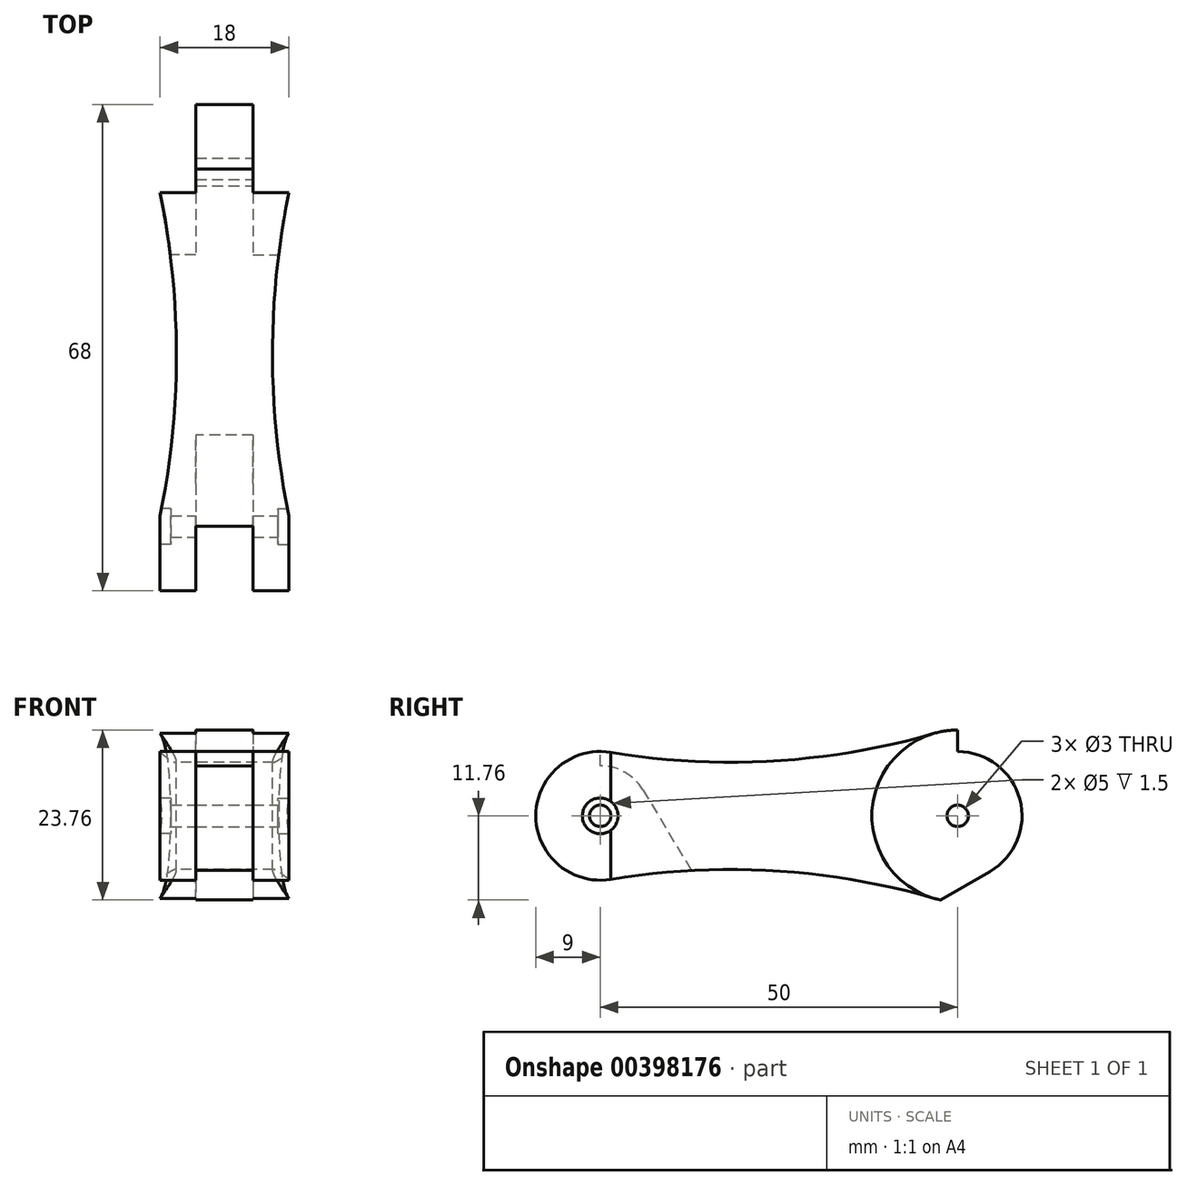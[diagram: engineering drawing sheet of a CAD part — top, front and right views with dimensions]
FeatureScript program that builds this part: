
annotation { "Feature Type Name" : "Feature", "Feature Type Description" : "" }
export const myFeature = defineFeature(function(context is Context, id is Id, definition is map)
    precondition{}
    {
        {
            var Q0;
            Q0=qCreatedBy(makeId("Right.planeOp"),FACE);
            var sketch = newSketch(context, id + "F0", { "sketchPlane" : qUnion([Q0])});
            skArc(sketch, "E0", {"start": v(1.47, 8.88) * mm, "mid": v(-9, 0) * mm, "end": v(1.47, -8.88) * mm});
            skLineSegment(sketch, "E1", {"start": v(-29.92, 0) * mm, "end": v(87.26, 0) * mm, "construction": true});
            skArc(sketch, "E2", {"start": v(46.67, -11.53) * mm, "mid": v(62, 0) * mm, "end": v(46.67, 11.53) * mm});
            skArc(sketch, "E3", {"start": v(1.47, 8.88) * mm, "mid": v(24.22, 7.68) * mm, "end": v(46.67, 11.53) * mm});
            skArc(sketch, "E4", {"start": v(46.67, -11.53) * mm, "mid": v(24.22, -7.68) * mm, "end": v(1.47, -8.88) * mm});
            skSolve(sketch);
        }
        {
            var Q0;
            Q0=qSketchRegion(id+"F0",true);
            extrude(context, id + "F1", {"entities" : qUnion([Q0]), "depth" : 5 * mm});
        }
        {
            var Q0;
            Q0=makeQuery(id+"F1.opExtrude","CAP_FACE",FACE,{"disambiguationData":[OSD([sQuery(id+"F0.wireOp",EDGE,"E0"),sQuery(id+"F0.wireOp",EDGE,"E2"),sQuery(id+"F0.wireOp",EDGE,"E3"),sQuery(id+"F0.wireOp",EDGE,"E4")])],"isStart":false});
            var sketch = newSketch(context, id + "F2", { "sketchPlane" : qUnion([Q0])});
            skArc(sketch, "E5.0", {"start": v(1.47, 8.88) * mm, "mid": v(24.22, 7.68) * mm, "end": v(46.67, 11.53) * mm});
            skArc(sketch, "E6.0", {"start": v(1.47, 8.88) * mm, "mid": v(0.74, 8.97) * mm, "end": v(0, 9) * mm});
            skArc(sketch, "E7.0", {"start": v(46.67, -11.53) * mm, "mid": v(29.88, -8.17) * mm, "end": v(12.76, -7.65) * mm});
            skArc(sketch, "E8.0", {"start": v(46.67, -11.53) * mm, "mid": v(62, 0) * mm, "end": v(46.67, 11.53) * mm});
            skArc(sketch, "E9", {"start": v(7, 0) * mm, "mid": v(4.95, 4.95) * mm, "end": v(0, 7) * mm});
            skLineSegment(sketch, "E10", {"start": v(0, 7) * mm, "end": v(0, 9) * mm});
            skLineSegment(sketch, "E11", {"start": v(0, 0) * mm, "end": v(34.92, 0) * mm, "construction": true});
            skLineSegment(sketch, "E12", {"start": v(6, 3.6) * mm, "end": v(12.76, -7.65) * mm});
            skPoint(sketch, "E13.orphan", {"position": v(7, 0) * mm});
            skSolve(sketch);
        }
        {
            var Q0;
            Q0=qSketchRegion(id+"F2",true);
            extrude(context, id + "F3", {"entities" : qUnion([Q0]), "operationType" : NewBodyOperationType.ADD, "depth" : 8 * mm});
        }
        {
            var Q0;
            Q0=makeQuery(id+"F3.opExtrude","CAP_FACE",FACE,{"disambiguationData":[OSD([sQuery(id+"F2.wireOp",EDGE,"E5.0"),sQuery(id+"F2.wireOp",EDGE,"E6.0"),sQuery(id+"F2.wireOp",EDGE,"E7.0"),sQuery(id+"F2.wireOp",EDGE,"E8.0"),sQuery(id+"F2.wireOp",EDGE,"E9"),sQuery(id+"F2.wireOp",EDGE,"E10"),sQuery(id+"F2.wireOp",EDGE,"JRJ70NO1-7vJe-Li3z-EIXT-plhISmGAnEbH")])],"isStart":false});
            var sketch = newSketch(context, id + "F4", { "sketchPlane" : qUnion([Q0])});
            skArc(sketch, "E14.0", {"start": v(0, 9) * mm, "mid": v(-8.97, -0.74) * mm, "end": v(1.47, -8.88) * mm});
            skArc(sketch, "E15.0", {"start": v(1.47, 8.88) * mm, "mid": v(24.22, 7.68) * mm, "end": v(46.67, 11.53) * mm});
            skArc(sketch, "E16.0", {"start": v(12.76, -7.65) * mm, "mid": v(7.1, -8.1) * mm, "end": v(1.47, -8.88) * mm});
            skArc(sketch, "E17.0", {"start": v(46.67, -11.53) * mm, "mid": v(29.88, -8.17) * mm, "end": v(12.76, -7.65) * mm});
            skArc(sketch, "E18.0", {"start": v(46.67, -11.53) * mm, "mid": v(62, 0) * mm, "end": v(46.67, 11.53) * mm});
            skArc(sketch, "E19.0", {"start": v(1.47, 8.88) * mm, "mid": v(0.74, 8.97) * mm, "end": v(0, 9) * mm});
            skSolve(sketch);
        }
        {
            var Q0;
            Q0=qSketchRegion(id+"F4",true);
            extrude(context, id + "F5", {"entities" : qUnion([Q0]), "operationType" : NewBodyOperationType.ADD, "depth" : 5 * mm});
        }
        {
            var Q0;
            Q0=makeQuery(id+"F5.opExtrude","CAP_FACE",FACE,{"disambiguationData":[OSD([sQuery(id+"F4.wireOp",EDGE,"E14.0"),sQuery(id+"F4.wireOp",EDGE,"E15.0"),sQuery(id+"F4.wireOp",EDGE,"E16.0"),sQuery(id+"F4.wireOp",EDGE,"E17.0"),sQuery(id+"F4.wireOp",EDGE,"E18.0"),sQuery(id+"F4.wireOp",EDGE,"E19.0")])],"isStart":false});
            var sketch = newSketch(context, id + "F6", { "sketchPlane" : qUnion([Q0])});
            skCircle(sketch, "E20", {"center": v(50, 0) * mm, "radius": 12 * mm});
            skSolve(sketch);
        }
        {
            var Q0;
            Q0=qSketchRegion(id+"F6",true);
            extrude(context, id + "F7", {"entities" : qUnion([Q0]), "operationType" : NewBodyOperationType.REMOVE, "oppositeDirection" : true, "depth" : 5 * mm});
        }
        {
            var Q0;
            Q0=makeQuery(id+"F1.opExtrude","CAP_FACE",FACE,{"disambiguationData":[OSD([sQuery(id+"F0.wireOp",EDGE,"E0"),sQuery(id+"F0.wireOp",EDGE,"E2"),sQuery(id+"F0.wireOp",EDGE,"E3"),sQuery(id+"F0.wireOp",EDGE,"E4")])],"isStart":true});
            var sketch = newSketch(context, id + "F8", { "sketchPlane" : qUnion([Q0])});
            skCircle(sketch, "E21", {"center": v(-50, 0) * mm, "radius": 12 * mm});
            skSolve(sketch);
        }
        {
            var Q0;
            Q0=qSketchRegion(id+"F8",true);
            extrude(context, id + "F9", {"entities" : qUnion([Q0]), "operationType" : NewBodyOperationType.REMOVE, "oppositeDirection" : true, "depth" : 5 * mm});
        }
        {
            var Q0;
            Q0=makeQuery(id+"F7.boolean.opBoolean","COPY",FACE,{"derivedFrom":makeQuery(id+"F7.opExtrude","CAP_FACE",FACE,{"disambiguationData":[OSD([sQuery(id+"F6.wireOp",EDGE,"E20")])],"isStart":false})});
            var sketch = newSketch(context, id + "F10", { "sketchPlane" : qUnion([Q0])});
            skArc(sketch, "E22", {"start": v(47.63, -11.76) * mm, "mid": v(61.94, -1.2) * mm, "end": v(50, 12) * mm});
            skArc(sketch, "E23", {"start": v(54.5, -7.8) * mm, "mid": v(58.7, 2.33) * mm, "end": v(50, 9) * mm});
            skLineSegment(sketch, "E24", {"start": v(50, 12) * mm, "end": v(50, 9) * mm});
            skLineSegment(sketch, "E25", {"start": v(54.5, -7.8) * mm, "end": v(47.63, -11.76) * mm});
            skSolve(sketch);
        }
        {
            var Q0;
            Q0=qSketchRegion(id+"F10",true);
            extrude(context, id + "F11", {"entities" : qUnion([Q0]), "operationType" : NewBodyOperationType.REMOVE, "endBound" : BoundingType.THROUGH_ALL, "oppositeDirection" : true, "depth" : 25 * mm});
        }
        {
            var Q0;
            Q0=makeQuery(id+"F5.opExtrude","CAP_FACE",FACE,{"disambiguationData":[OSD([sQuery(id+"F4.wireOp",EDGE,"E14.0"),sQuery(id+"F4.wireOp",EDGE,"E15.0"),sQuery(id+"F4.wireOp",EDGE,"E16.0"),sQuery(id+"F4.wireOp",EDGE,"E18.0"),sQuery(id+"F4.wireOp",EDGE,"E19.0"),sQuery(id+"F4.wireOp",EDGE,"E17.0")])],"isStart":false});
            var sketch = newSketch(context, id + "F12", { "sketchPlane" : qUnion([Q0])});
            skCircle(sketch, "E26", {"center": v(0, 0) * mm, "radius": 1.5 * mm});
            skCircle(sketch, "E27", {"center": v(50, 0) * mm, "radius": 1.5 * mm});
            skSolve(sketch);
        }
        {
            var Q0;
            Q0=qSketchRegion(id+"F12",true);
            extrude(context, id + "F13", {"entities" : qUnion([Q0]), "operationType" : NewBodyOperationType.REMOVE, "endBound" : BoundingType.THROUGH_ALL, "oppositeDirection" : true, "depth" : 25 * mm});
        }
        {
            var Q0;
            Q0=makeQuery(id+"F5.opExtrude","CAP_FACE",FACE,{"disambiguationData":[OSD([sQuery(id+"F4.wireOp",EDGE,"E14.0"),sQuery(id+"F4.wireOp",EDGE,"E15.0"),sQuery(id+"F4.wireOp",EDGE,"E16.0"),sQuery(id+"F4.wireOp",EDGE,"E18.0"),sQuery(id+"F4.wireOp",EDGE,"E19.0"),sQuery(id+"F4.wireOp",EDGE,"E17.0")])],"isStart":false});
            var sketch = newSketch(context, id + "F14", { "sketchPlane" : qUnion([Q0])});
            skCircle(sketch, "E28", {"center": v(0, 0) * mm, "radius": 2.5 * mm});
            skSolve(sketch);
        }
        {
            var Q0;
            Q0=qSketchRegion(id+"F14",true);
            extrude(context, id + "F15", {"entities" : qUnion([Q0]), "operationType" : NewBodyOperationType.REMOVE, "oppositeDirection" : true, "depth" : 1.5 * mm});
        }
        {
            var Q0;
            Q0=makeQuery(id+"F1.opExtrude","CAP_FACE",FACE,{"disambiguationData":[OSD([sQuery(id+"F0.wireOp",EDGE,"E0"),sQuery(id+"F0.wireOp",EDGE,"E2"),sQuery(id+"F0.wireOp",EDGE,"E3"),sQuery(id+"F0.wireOp",EDGE,"E4")])],"isStart":true});
            var sketch = newSketch(context, id + "F16", { "sketchPlane" : qUnion([Q0])});
            skCircle(sketch, "E29", {"center": v(0, 0) * mm, "radius": 2.5 * mm});
            skSolve(sketch);
        }
        {
            var Q0;
            Q0=qSketchRegion(id+"F16",true);
            extrude(context, id + "F17", {"entities" : qUnion([Q0]), "operationType" : NewBodyOperationType.REMOVE, "oppositeDirection" : true, "depth" : 1.5 * mm});
        }
        {
            var Q0;
            Q0=qCreatedBy(makeId("Top.planeOp"),FACE);
            var sketch = newSketch(context, id + "F18", { "sketchPlane" : qUnion([Q0])});
            skCircle(sketch, "E30", {"center": v(-111, 24.07) * mm, "radius": 113.28 * mm});
            skCircle(sketch, "E31", {"center": v(129, 24.07) * mm, "radius": 113.28 * mm});
            skSolve(sketch);
        }
        {
            var Q0;
            Q0=qSketchRegion(id+"F18",true);
            extrude(context, id + "F19", {"entities" : qUnion([Q0]), "operationType" : NewBodyOperationType.REMOVE, "endBound" : BoundingType.SYMMETRIC, "oppositeDirection" : true, "depth" : 25 * mm});
        }
    });
